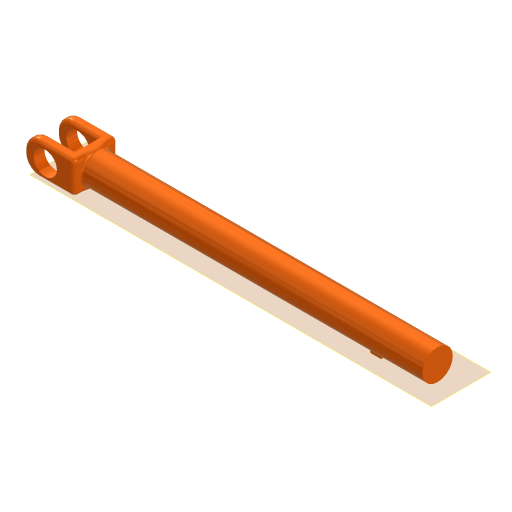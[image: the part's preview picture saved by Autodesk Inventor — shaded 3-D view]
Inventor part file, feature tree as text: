
AUTODESK INVENTOR PART (.ipt)
format: ipt  version: 2024 (Build 280153000, 153)  size: 256,512 bytes
history: native  units: mm
features: sketch x7, extrude x5, fillet x4, other x4
ambient origin geometry x8: Origin, YZ Plane, XZ Plane, XY Plane, X Axis, Y Axis, Z Axis, Center Point
bodies: Solido1 (feature_tree)
feature tree (20):
  sketch  "Schizzo1"
  extrude  "Estrusione1"  Depth=18.0mm
  extrude  "Estrusione4"  Depth=136.5mm
  extrude  "Estrusione5"  Depth=7.0mm
  sketch  "Schizzo9"
  extrude  "Estrusione6"  Depth=14.0mm
  fillet  "Raccordo1"  Radius=157.07mm
  fillet  "Raccordo2"  Radius=20.0mm
  other  "Raccordo faccia1"
  fillet  "Raccordo3"  Radius=10.0mm
  fillet  "Raccordo4"  Radius=15.0mm
  other  "Piano di lavoro3"
  other  "Piano di lavoro4"
  other  "Piano di lavoro5"
  extrude  "Estrusione10"  Depth=7.5mm
  sketch  "Schizzo2"
  sketch  "Schizzo7"
  sketch  "Schizzo8"
  sketch  "Schizzo10"
  sketch  "Schizzo15"
